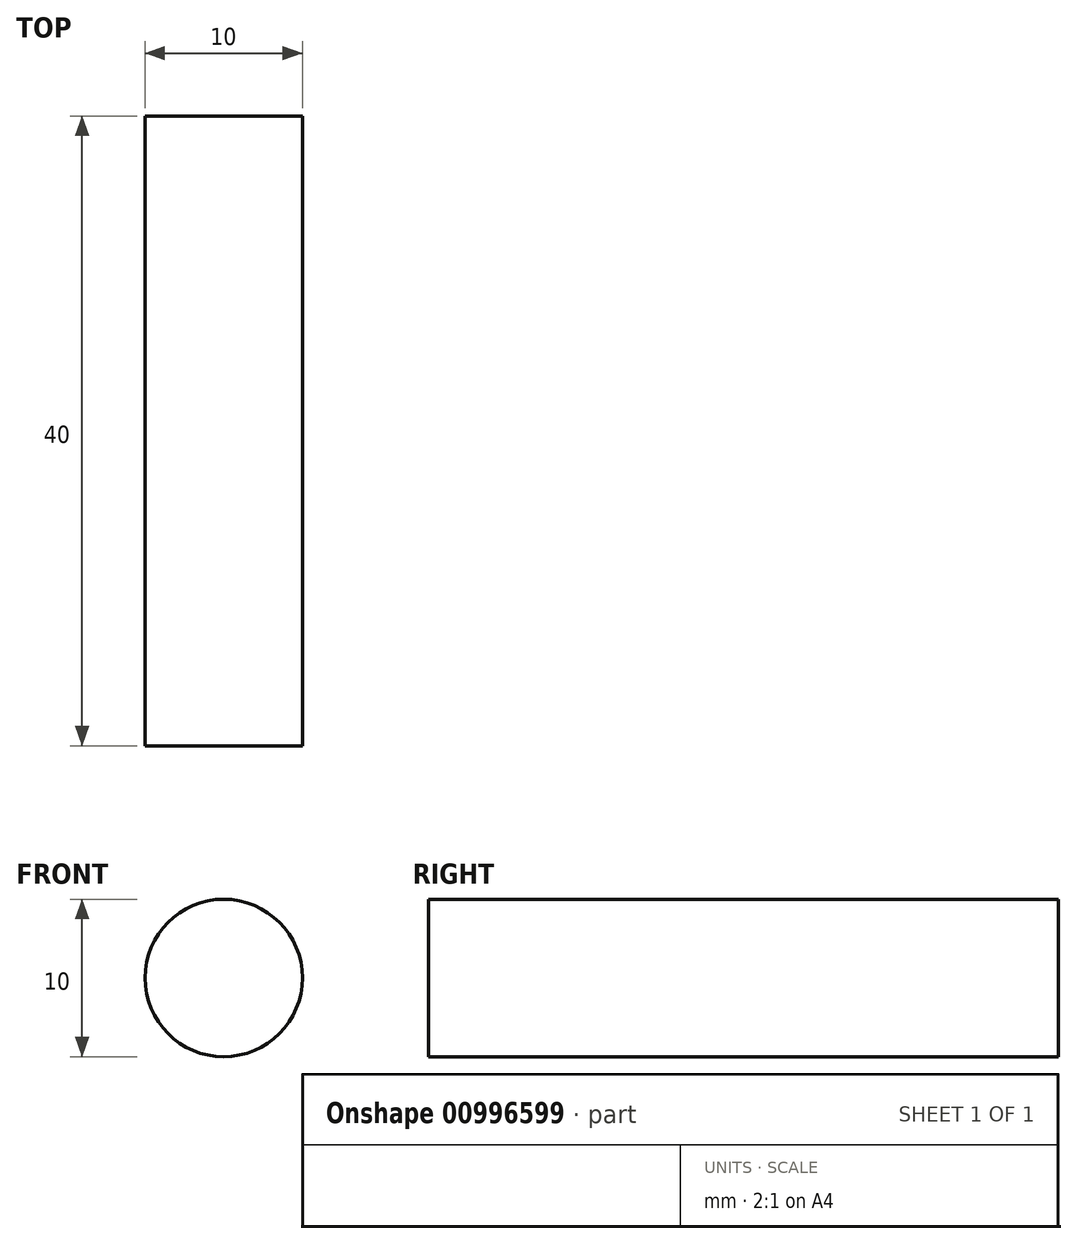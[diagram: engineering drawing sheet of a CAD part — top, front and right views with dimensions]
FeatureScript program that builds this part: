
annotation { "Feature Type Name" : "Feature", "Feature Type Description" : "" }
export const myFeature = defineFeature(function(context is Context, id is Id, definition is map)
    precondition{}
    {
        {
            var Q0;
            Q0=qCreatedBy(makeId("Front.planeOp"),FACE);
            var sketch = newSketch(context, id + "F0", { "sketchPlane" : qUnion([Q0])});
            skCircle(sketch, "E0", {"center": v(0, 0) * mm, "radius": 5 * mm});
            skSolve(sketch);
        }
        {
            var Q0;
            Q0=makeQuery(id+"F0.imprint","IMPRINT",FACE,{"disambiguationData":[TD([[makeQuery(id+"F0.imprint","IMPRINT",EDGE,{"derivedFrom":sQuery(id+"F0.wireOp",EDGE,"E0")}),1.0]])]});
            extrude(context, id + "F1", {"entities" : qUnion([Q0]), "depth" : 40 * mm, "offsetDistance" : 25 * mm});
        }
    });
